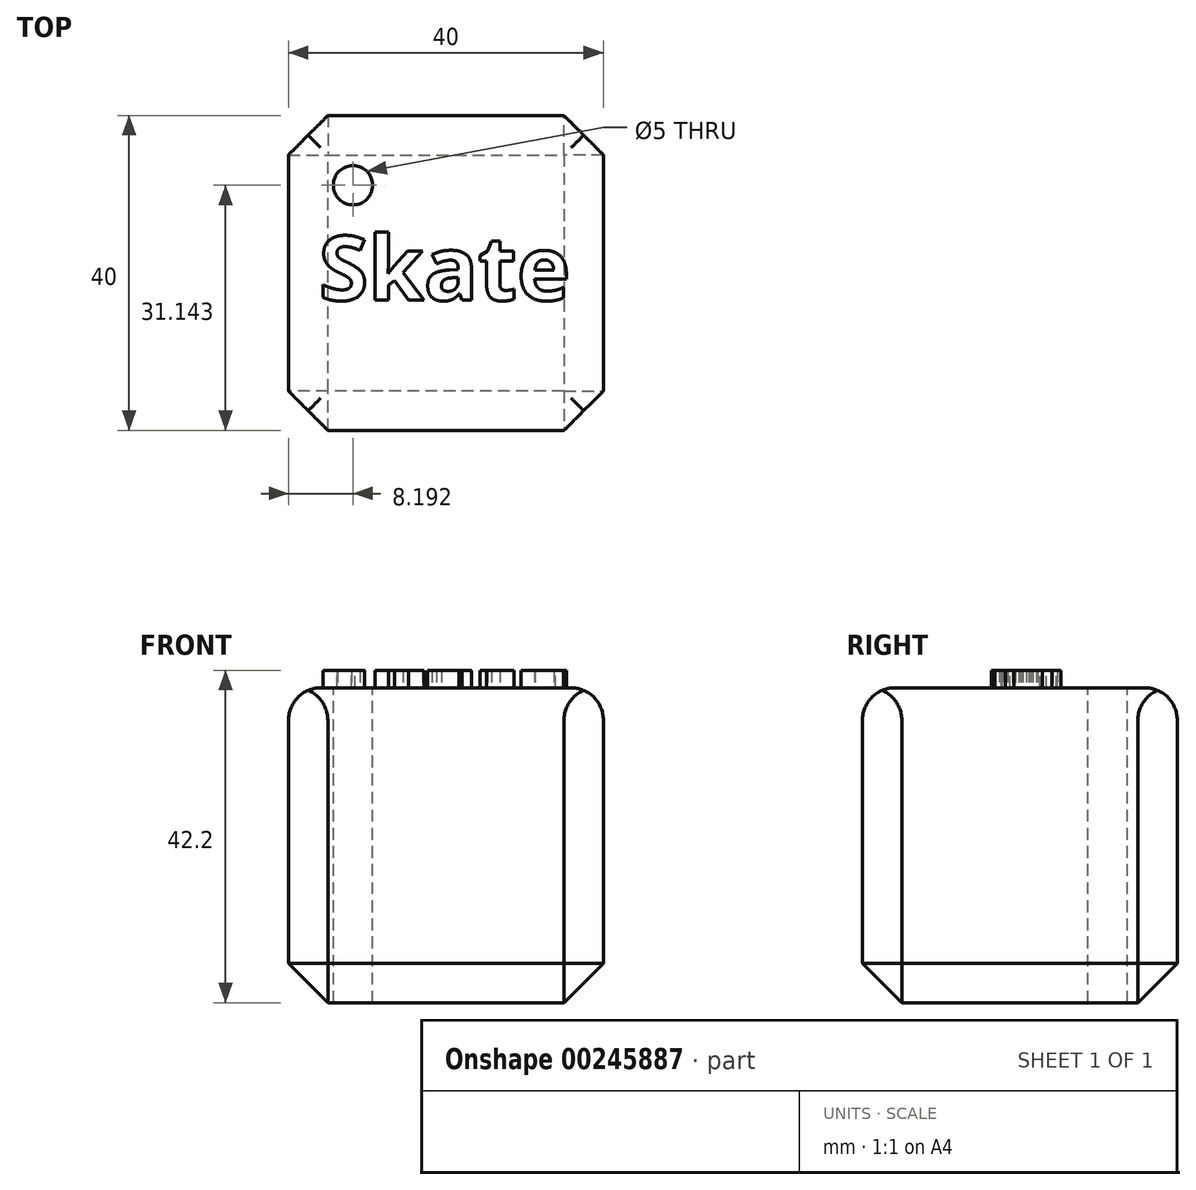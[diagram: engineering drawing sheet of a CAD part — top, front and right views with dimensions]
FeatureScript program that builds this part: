
annotation { "Feature Type Name" : "Feature", "Feature Type Description" : "" }
export const myFeature = defineFeature(function(context is Context, id is Id, definition is map)
    precondition{}
    {
        {
            var Q0;
            Q0=qCreatedBy(makeId("Top.planeOp"),FACE);
            var sketch = newSketch(context, id + "F0", { "sketchPlane" : qUnion([Q0])});
            skLineSegment(sketch, "E0", {"start": v(-54.53, 40) * mm, "end": v(-54.53, 0) * mm});
            skLineSegment(sketch, "E1", {"start": v(-54.53, 40) * mm, "end": v(-14.53, 40) * mm});
            skLineSegment(sketch, "E2", {"start": v(-54.53, 0) * mm, "end": v(-14.53, 0) * mm});
            skLineSegment(sketch, "E3", {"start": v(-14.53, 40) * mm, "end": v(-14.53, 0) * mm});
            skSolve(sketch);
        }
        {
            var Q0;
            Q0=makeQuery(id+"F0.imprint","IMPRINT",FACE,{"disambiguationData":[TD([[makeQuery(id+"F0.imprint","IMPRINT",EDGE,{"derivedFrom":sQuery(id+"F0.wireOp",EDGE,"E0")}),1.0]])]});
            extrude(context, id + "F1", {"entities" : qUnion([Q0]), "depth" : 40 * mm});
        }
        {
            var Q0;
            Q0=makeQuery(id+"F1.opExtrude","CAP_FACE",FACE,{"disambiguationData":[OSD([sQuery(id+"F0.wireOp",EDGE,"E0"),sQuery(id+"F0.wireOp",EDGE,"E1"),sQuery(id+"F0.wireOp",EDGE,"E2"),sQuery(id+"F0.wireOp",EDGE,"E3")])],"isStart":false});
            var sketch = newSketch(context, id + "F2", { "sketchPlane" : qUnion([Q0])});
            skCircle(sketch, "E4", {"center": v(-34.51, 19.24) * mm, "radius": 17.57 * mm});
            skCircle(sketch, "E5", {"center": v(-34.51, 19.24) * mm, "radius": 14.68 * mm});
            skCircle(sketch, "E6", {"center": v(-34.51, 19.24) * mm, "radius": 11.9 * mm});
            skCircle(sketch, "E7", {"center": v(-34.51, 19.24) * mm, "radius": 9.63 * mm});
            skCircle(sketch, "E8", {"center": v(-34.51, 19.24) * mm, "radius": 7.04 * mm});
            skSolve(sketch);
        }
        {
            var Q0;
            Q0=makeQuery(id+"F2.imprint","IMPRINT",FACE,{"disambiguationData":[TD([[makeQuery(id+"F2.imprint","IMPRINT",EDGE,{"derivedFrom":sQuery(id+"F2.wireOp",EDGE,"E8")}),1.0]])]});
            var Q1;
            Q1=makeQuery(id+"F2.imprint","IMPRINT",FACE,{"disambiguationData":[TD([[makeQuery(id+"F2.imprint","IMPRINT",EDGE,{"derivedFrom":sQuery(id+"F2.wireOp",EDGE,"E7")}),1.0]])]});
            var Q2;
            Q2=makeQuery(id+"F2.imprint","IMPRINT",FACE,{"disambiguationData":[TD([[makeQuery(id+"F2.imprint","IMPRINT",EDGE,{"derivedFrom":sQuery(id+"F2.wireOp",EDGE,"E6")}),1.0]])]});
            var Q3;
            Q3=makeQuery(id+"F2.imprint","IMPRINT",FACE,{"disambiguationData":[TD([[makeQuery(id+"F2.imprint","IMPRINT",EDGE,{"derivedFrom":sQuery(id+"F2.wireOp",EDGE,"E5")}),1.0]])]});
            var Q4;
            Q4=makeQuery(id+"F2.imprint","IMPRINT",FACE,{"disambiguationData":[TD([[makeQuery(id+"F2.imprint","IMPRINT",EDGE,{"derivedFrom":sQuery(id+"F2.wireOp",EDGE,"E4")}),1.0]])]});
            extrude(context, id + "F3", {"entities" : qUnion([Q0, Q1, Q2, Q3, Q4]), "operationType" : NewBodyOperationType.ADD, "oppositeDirection" : true, "depth" : 4.2 * mm});
        }
        {
            var Q0;
            Q0 = qSketchRegion(id + "F2", true);
            extrude(context, id + "F4", {"entities" : qUnion([Q0]), "operationType" : NewBodyOperationType.ADD, "oppositeDirection" : true, "depth" : 10.5 * mm});
        }
        {
            var Q0;
            Q0=makeQuery(id+"F1.opExtrude","CAP_FACE",FACE,{"disambiguationData":[OSD([sQuery(id+"F0.wireOp",EDGE,"E0"),sQuery(id+"F0.wireOp",EDGE,"E1"),sQuery(id+"F0.wireOp",EDGE,"E2"),sQuery(id+"F0.wireOp",EDGE,"E3")])],"isStart":false});
            fillet(context, id + "F5", {"entities" : qUnion([Q0]), "radius" : 4.1 * mm, "tangentPropagation" : true, "allowEdgeOverflow" : false});
        }
        {
            var Q0;
            Q0=makeQuery(id+"F1.opExtrude","SWEPT_FACE",FACE,{"disambiguationData":[OSD([sQuery(id+"F0.wireOp",EDGE,"E2")])]});
            var Q1;
            Q1=makeQuery(id+"F1.opExtrude","SWEPT_FACE",FACE,{"disambiguationData":[OSD([sQuery(id+"F0.wireOp",EDGE,"E0")])]});
            var Q2;
            Q2=makeQuery(id+"F1.opExtrude","SWEPT_FACE",FACE,{"disambiguationData":[OSD([sQuery(id+"F0.wireOp",EDGE,"E3")])]});
            var Q3;
            Q3=makeQuery(id+"F1.opExtrude","SWEPT_FACE",FACE,{"disambiguationData":[OSD([sQuery(id+"F0.wireOp",EDGE,"E1")])]});
            chamfer(context, id + "F6", {"entities" : qUnion([Q0, Q1, Q2, Q3]), "width" : 5 * mm, "tangentPropagation" : true});
        }
        {
            var Q0;
            Q0=makeQuery(id+"F1.opExtrude","CAP_FACE",FACE,{"disambiguationData":[OSD([sQuery(id+"F0.wireOp",EDGE,"E0"),sQuery(id+"F0.wireOp",EDGE,"E1"),sQuery(id+"F0.wireOp",EDGE,"E2"),sQuery(id+"F0.wireOp",EDGE,"E3")])],"isStart":false});
            var sketch = newSketch(context, id + "F7", { "sketchPlane" : qUnion([Q0])});
            skCircle(sketch, "E9", {"center": v(-46.34, 31.14) * mm, "radius": 3.3 * mm});
            skSolve(sketch);
        }
        {
            var Q0;
            Q0=sQuery(id+"F7.wireOp",VERTEX,"E9.center");
            var Q1;
            Q1=makeQuery(id+"F1.opExtrude","SWEPT_BODY",BODY,{"disambiguationData":[OSD([sQuery(id+"F0.wireOp",EDGE,"E0"),sQuery(id+"F0.wireOp",EDGE,"E1"),sQuery(id+"F0.wireOp",EDGE,"E2"),sQuery(id+"F0.wireOp",EDGE,"E3")])]});
            hole(context, id + "F8", {"style" : HoleStyle.SIMPLE, "endStyle" : HoleEndStyle.THROUGH, "holeDiameter" : 5 * mm, "tappedDepth" : 12 * mm, "tapClearance" : 3, "locations" : qUnion([Q0]), "scope" : qUnion([Q1])});
        }
        {
            var Q0;
            Q0=makeQuery(id+"F1.opExtrude","CAP_FACE",FACE,{"disambiguationData":[OSD([sQuery(id+"F0.wireOp",EDGE,"E0"),sQuery(id+"F0.wireOp",EDGE,"E1"),sQuery(id+"F0.wireOp",EDGE,"E2"),sQuery(id+"F0.wireOp",EDGE,"E3")])],"isStart":false});
            var sketch = newSketch(context, id + "F9", { "sketchPlane" : qUnion([Q0])});
            skText(sketch, "E10", { "text": "Skate", "fontName": "OpenSans-Bold.ttf"});
            const initialGuessF9  = {"E10": [-0.05068, 0.01653, 1, 0, 0.00821]};
            skSetInitialGuess(sketch, initialGuessF9);
            skSolve(sketch);
        }
        {
            var Q0;
            Q0 = qSketchRegion(id + "F9", true);
            extrude(context, id + "F10", {"entities" : qUnion([Q0]), "operationType" : NewBodyOperationType.ADD, "depth" : 2.2 * mm});
        }
    });
